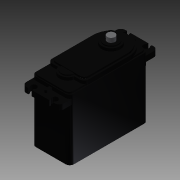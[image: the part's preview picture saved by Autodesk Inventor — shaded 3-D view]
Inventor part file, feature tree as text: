
AUTODESK INVENTOR PART (.ipt)
format: ipt  version: 2015 (Build 190159000, 159)  size: 407,552 bytes
history: native  units: in
note: dims shown in document units (in); Inventor stores cm internally (conversion verified against a paired STEP export)
features: extrude x18, sketch x18, projected_geometry x4, fillet x2, plane x1
ambient origin geometry x8: Origin, YZ Plane, XZ Plane, XY Plane, X Axis, Y Axis, Z Axis, Center Point
bodies: Solid1 (feature_tree)
feature tree (43):
  extrude  "Extrusion1"  Depth=1.832in
  extrude  "Extrusion2"  Depth=1.04in
  extrude  "Extrusion3"  Depth=0.04in TaperAngle=0.0deg
  extrude  "Extrusion4"  Depth=0.449in
  extrude  "Extrusion5"  Depth=0.0835in
  fillet  "Fillet1"  Radius=0.0835in
  plane  "Work Plane1"
  extrude  "Extrusion6"  Depth=0.9645in
  fillet  "Fillet2"  Radius=0.0175in
  extrude  "Extrusion7"  [1 undecoded]
  extrude  "Extrusion8"  Depth=2.907in
  extrude  "Extrusion9"  Depth=0.125in
  extrude  "Extrusion10"  Depth=0.149in
  extrude  "Extrusion11"  Depth=0.17in
  extrude  "Extrusion12"  Depth=0.1575in TaperAngle=0.0deg
  extrude  "Extrusion13"  Depth=0.1035in
  extrude  "Extrusion14"  Depth=0.08in
  extrude  "Extrusion15"  Depth=0.0645in TaperAngle=0.0deg
  extrude  "Extrusion16"  Depth=0.077in TaperAngle=0.0deg
  extrude  "Extrusion17"  Depth=0.025in TaperAngle=0.0deg
  extrude  "Extrusion18"  Depth=0.127in TaperAngle=0.0deg
  sketch  "Sketch1"  dims[d0=2.309in d1=1.832in]
  sketch  "Sketch2"  dims[d2=1.121in d3=0.0in d4=1.04in]
  sketch  "Sketch3"  dims[d5=2.2635in d7=0.04in d8=0.0in]
  projected_geometry  "Projected Loop1"
  sketch  "Sketch4"  dims[d9=0.026in d10=0.449in]
  sketch  "Sketch5"  dims[d12=0.488in d13=0.189in d14=0.0835in d15=0.0in]
  sketch  "Sketch6"  dims[d16=0.044in d17=0.0in d18=0.9645in d19=0.0175in d20=0.0in]
  projected_geometry  "Projected Loop2"
  sketch  "Sketch7"  dims[d21=0.125in d22=-0.103in]
  sketch  "Sketch8"  dims[d23=1.0915in d24=2.907in]
  sketch  "Sketch9"  dims[d25=0.1575in d26=0.0in d27=0.125in]
  sketch  "Sketch10"  dims[d28=0.149in d29=0.149in]
  sketch  "Sketch11"  dims[d30=0.1995in d31=0.17in]
  sketch  "Sketch12"  dims[d32=0.17in d33=0.1575in d34=0.0in]
  sketch  "Sketch13"  dims[d35=0.184in d36=0.1035in]
  sketch  "Sketch14"  dims[d37=0.1575in d38=0.0in d39=0.08in]
  sketch  "Sketch15"  dims[d40=0.1345in d41=0.0645in d42=0.0in]
  sketch  "Sketch16"  dims[d43=0.5455in d44=0.077in d45=0.0in]
  projected_geometry  "Projected Loop4"
  sketch  "Sketch18"  dims[d46=0.43in d47=0.025in d48=0.0in]
  sketch  "Sketch20"  dims[d49=0.225in d50=0.127in d51=0.0in d52=0.1405in d53=0.1465in d54=0.293in d55=0.137in d56=0.241in d57=-0.0687in d58=1.0in d59=0.0in d60=1.0in d61=0.0in d62=1.0in d63=0.0in d64=0.0645in d65=0.0in d66=0.0645in d67=0.0in]
  projected_geometry  "Projected Loop5"
note: 1 required parameter value undecoded (feature->parameter linkage not recoverable at this tier; creation-order binding heuristic only, values carry confidence <= 0.55)
